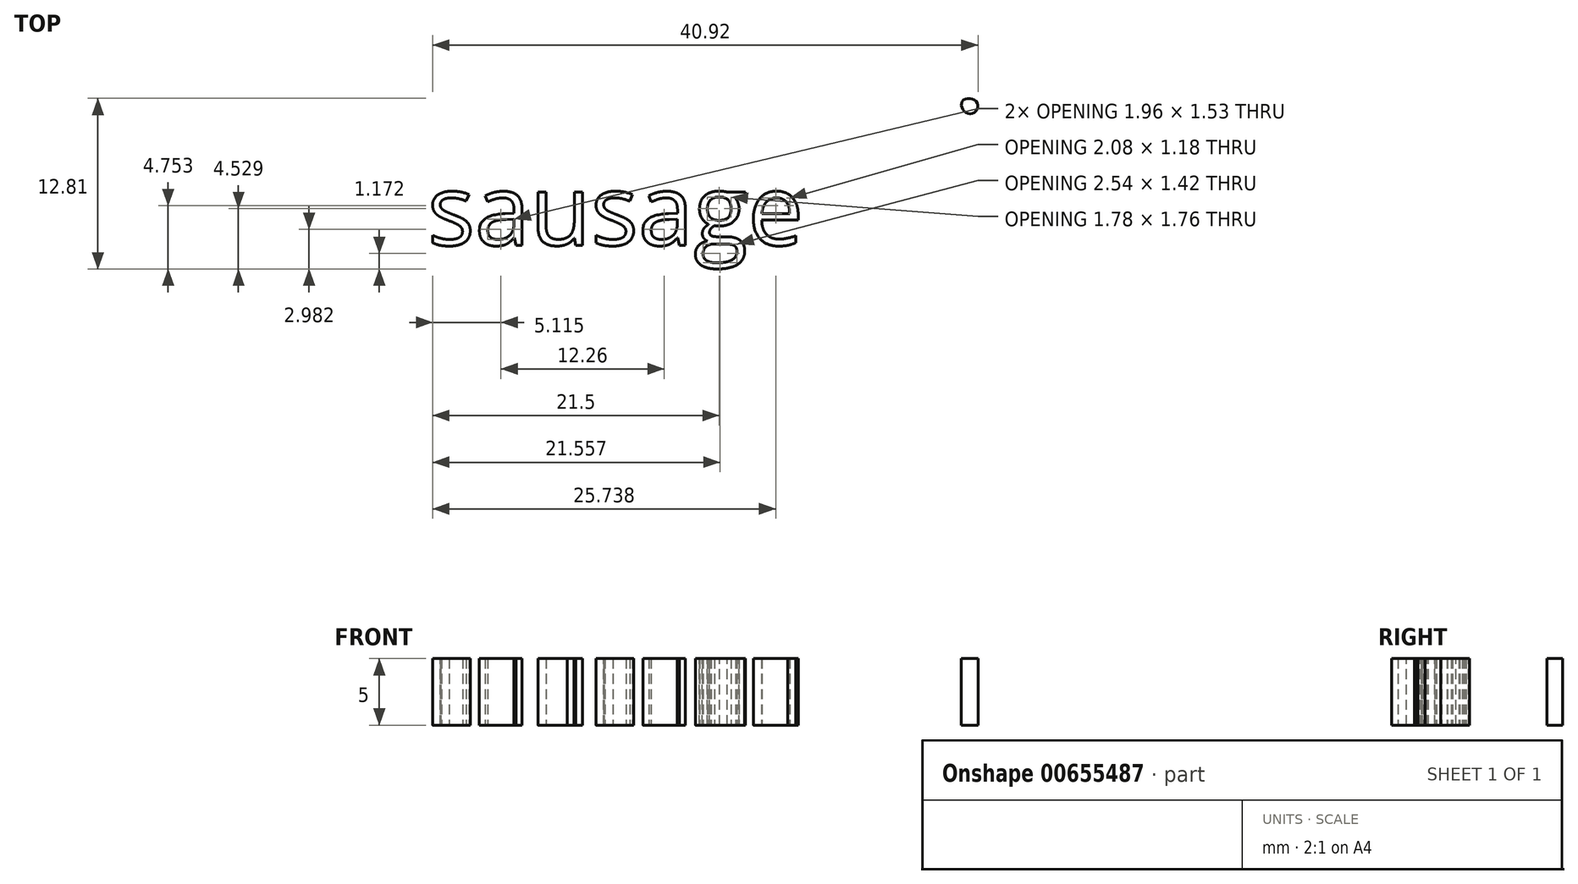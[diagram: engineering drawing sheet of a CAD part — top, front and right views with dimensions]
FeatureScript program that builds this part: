
annotation { "Feature Type Name" : "Feature", "Feature Type Description" : "" }
export const myFeature = defineFeature(function(context is Context, id is Id, definition is map)
    precondition{}
    {
        {
            var Q0;
            Q0=qCreatedBy(makeId("Top.planeOp"),FACE);
            var sketch = newSketch(context, id + "F0", { "sketchPlane" : qUnion([Q0])});
            skFitSpline(sketch, "E0", {"points": [v(-60.55, 42.25) * mm, v(-60.68, 42.88) * mm, v(-61.43, 42.88) * mm, v(-62.61, 43.44) * mm, v(-62.36, 45.19) * mm, v(-61.43, 45.31) * mm, v(-61.05, 46.12) * mm, v(-59.8, 46) * mm, v(-59.5, 43.88) * mm, v(-57.43, 45.37) * mm, v(-53.5, 45.44) * mm, v(-51.45, 44.25) * mm, v(-46.95, 41.7) * mm, v(-40.1, 40.26) * mm, v(-30.6, 39.63) * mm, v(-23.19, 41.38) * mm, v(-17.76, 44.06) * mm, v(-13.9, 45.81) * mm, v(-9.77, 44.31) * mm, v(-9.03, 44.69) * mm, v(-9.03, 44.69) * mm, v(-7.73, 45.56) * mm, v(-6.45, 44.8) * mm, v(-6.45, 43.25) * mm, v(-8.03, 42.2) * mm, v(-7.84, 40.94) * mm, v(-7.84, 37.26) * mm, v(-11.65, 33.27) * mm, v(-20.44, 29.47) * mm, v(-33.42, 27.97) * mm, v(-47.64, 29.34) * mm, v(-58.43, 33.9) * mm, v(-61.24, 37.7) * mm, v(-60.55, 42.25) * mm]});
            skText(sketch, "E1", { "text": "sausage", "fontName": "OpenSans-Regular.ttf"});
            skFitSpline(sketch, "E2", {"points": [v(-12.29, 42.99) * mm, v(-12.4, 42.39) * mm, v(-11.8, 41.94) * mm, v(-11.21, 42.39) * mm, v(-11.48, 43) * mm, v(-12.29, 42.99) * mm]});
            skFitSpline(sketch, "E3", {"points": [v(-4.97, 46.94) * mm, v(-4.87, 45.75) * mm, v(-3.48, 45.75) * mm, v(-3.29, 46.74) * mm, v(-3.48, 47.54) * mm, v(-4.97, 46.94) * mm]});
            skFitSpline(sketch, "E4", {"points": [v(-3.58, 49.52) * mm, v(-3.09, 48.73) * mm, v(-2.8, 48.73) * mm, v(-2.2, 49.52) * mm, v(-2.1, 50.4) * mm, v(-2.2, 51) * mm, v(-2.5, 50.6) * mm, v(-3.58, 49.52) * mm]});
            const initialGuessF0  = {"E1": [-0.0525, 0.03209, 1, 0, 0.00536]};
            skSetInitialGuess(sketch, initialGuessF0);
            skSolve(sketch);
        }
        {
            var Q0;
            Q0 = qSketchRegion(id + "F0", true);
            extrude(context, id + "F1", {"entities" : qUnion([Q0]), "depth" : 5 * mm, "offsetDistance" : 25.4 * mm});
        }
        {
            var Q0;
            Q0=makeQuery(id+"F1.opExtrude","SWEPT_BODY",BODY,{"disambiguationData":[OSD([sQuery(id+"F0.wireOp",EDGE,"E3")])]});
            deleteBodies(context, id + "F2", {"entities" : qUnion([Q0])});
        }
        {
            var Q0;
            Q0=makeQuery(id+"F1.opExtrude","SWEPT_BODY",BODY,{"disambiguationData":[OSD([sQuery(id+"F0.wireOp",EDGE,"E4")])]});
            deleteBodies(context, id + "F3", {"entities" : qUnion([Q0])});
        }
    });
